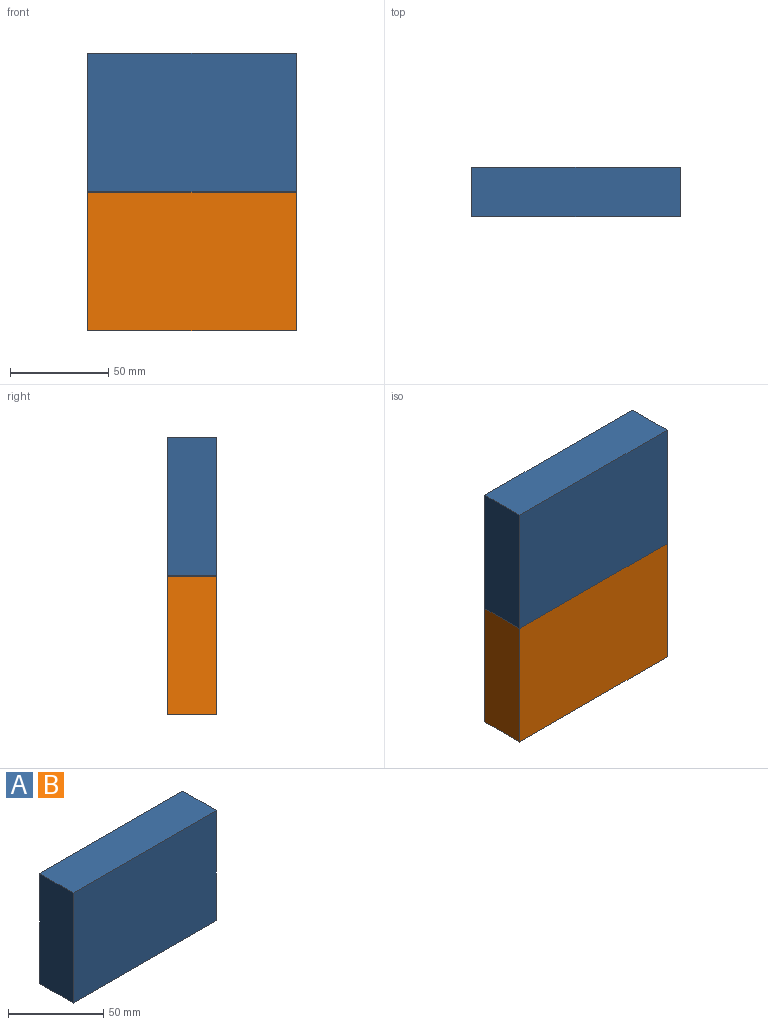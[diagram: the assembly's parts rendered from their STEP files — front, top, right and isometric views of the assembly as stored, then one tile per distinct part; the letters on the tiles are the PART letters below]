
ASSEMBLY  parts=2 mates=1
PART A: 6 faces, bbox 106.1x25x70.6 mm
  f0: plane 106.07x25mm, normal (0,0,1), area 2651.8mm2, adj f1,f3,f4,f5
  f1: plane 70.6x25mm, normal (-1,0,0), area 1765.1mm2, adj f0,f2,f4,f5
  f2: plane 106.07x25mm, normal (0,0,-1), area 2651.8mm2, adj f1,f3,f4,f5
  f3: plane 70.6x25mm, normal (1,0,0), area 1765.1mm2, adj f0,f2,f4,f5
  f4: plane 106.07x70.6mm, normal (0,-1,0), area 7489mm2, adj f0,f1,f2,f3
  f5: plane 106.07x70.6mm, normal (0,1,0), area 7489mm2, adj f0,f1,f2,f3
PART B: same geometry as A
PLACE A rot(axis=(1,0,0),180deg) t=(53.09,39.38,129.42)mm
PLACE B t=(53.09,64.38,50.59)mm
MATE fastened A.f0 <-> B.f0  axis (0,0,-1) through (-14.63,51.88,90)mm
